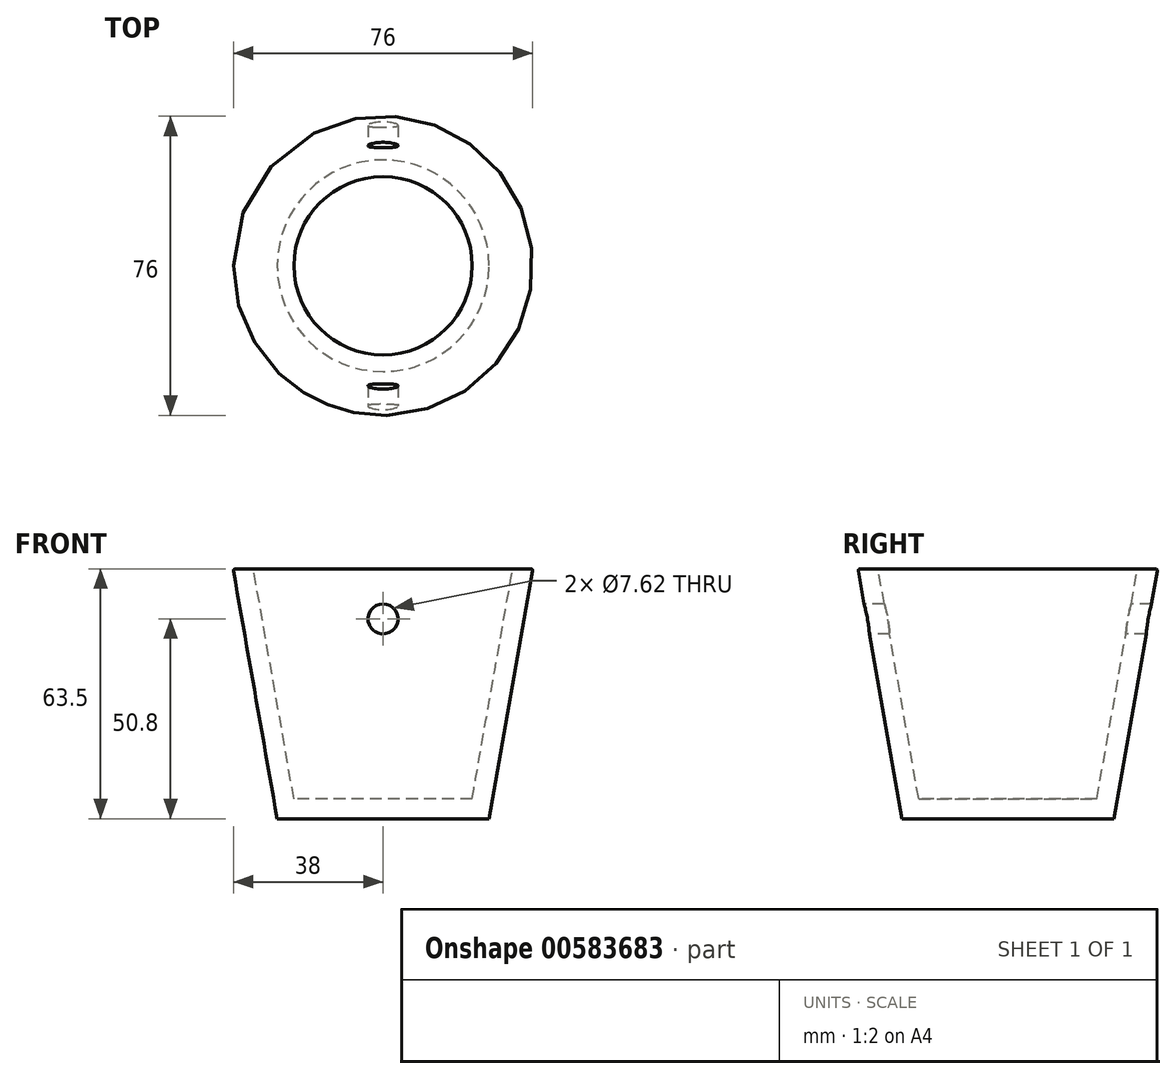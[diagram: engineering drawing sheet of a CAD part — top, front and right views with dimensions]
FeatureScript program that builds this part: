
annotation { "Feature Type Name" : "Feature", "Feature Type Description" : "" }
export const myFeature = defineFeature(function(context is Context, id is Id, definition is map)
    precondition{}
    {
        {
            var Q0;
            Q0=qCreatedBy(makeId("Front.planeOp"),FACE);
            var sketch = newSketch(context, id + "F0", { "sketchPlane" : qUnion([Q0])});
            skLineSegment(sketch, "E0", {"start": v(0, 63.5) * mm, "end": v(-38.1, 63.5) * mm});
            skLineSegment(sketch, "E1", {"start": v(-38.1, 63.5) * mm, "end": v(-26.9, 0) * mm});
            skLineSegment(sketch, "E2", {"start": v(-26.9, 0) * mm, "end": v(0, 0) * mm});
            skLineSegment(sketch, "E3", {"start": v(0, 0) * mm, "end": v(0, 63.5) * mm});
            skSolve(sketch);
        }
        {
            var Q0;
            Q0=makeQuery(id+"F0.imprint","IMPRINT",FACE,{"disambiguationData":[TD([[makeQuery(id+"F0.imprint","IMPRINT",EDGE,{"derivedFrom":sQuery(id+"F0.wireOp",EDGE,"E0")}),1.0]])]});
            var Q1;
            Q1=sQuery(id+"F0.wireOp",EDGE,"E3");
            revolve(context, id + "F1", {"entities" : qUnion([Q0]), "axis" : qUnion([Q1]), "revolveType" : RevolveType.FULL});
        }
        {
            var Q0;
            Q0=makeQuery(id+"F1.opRevolve","SWEPT_FACE",FACE,{"disambiguationData":[OSD([sQuery(id+"F0.wireOp",EDGE,"E0")])]});
            shell(context, id + "F2", {"entities" : qUnion([Q0]), "thickness" : 5.08 * mm});
        }
        {
            var Q0;
            Q0=qCreatedBy(makeId("Front.planeOp"),FACE);
            var sketch = newSketch(context, id + "F3", { "sketchPlane" : qUnion([Q0])});
            skLineSegment(sketch, "E4.0", {"start": v(38.1, 63.5) * mm, "end": v(-38.1, 63.5) * mm});
            skLineSegment(sketch, "E5", {"start": v(0, 63.5) * mm, "end": v(0, 50.8) * mm, "construction": true});
            skCircle(sketch, "E6", {"center": v(0, 50.8) * mm, "radius": 3.81 * mm});
            skSolve(sketch);
        }
        {
            var Q0;
            Q0 = qSketchRegion(id + "F3", true);
            extrude(context, id + "F4", {"entities" : qUnion([Q0]), "operationType" : NewBodyOperationType.REMOVE, "oppositeDirection" : true, "depth" : 50.3 * mm, "offsetDistance" : 25.4 * mm, "hasSecondDirection" : true, "secondDirectionOppositeDirection" : false, "secondDirectionDepth" : 74.17 * mm});
        }
        {
            var Q0;
            Q0=makeQuery(id+"F2.opShell","OFFSET_EDGE",EDGE,{"disambiguationData":[OSD([sQuery(id+"F0.wireOp",EDGE,"E0"),sQuery(id+"F0.wireOp",EDGE,"E1")])]});
            var Q1;
            Q1=makeQuery(id+"F1.opRevolve","SWEPT_EDGE",EDGE,{"disambiguationData":[OSD([sQuery(id+"F0.wireOp",EDGE,"E0"),sQuery(id+"F0.wireOp",EDGE,"E1")])]});
            fillet(context, id + "F5", {"entities" : qUnion([Q0, Q1]), "radius" : 0.5 * mm, "tangentPropagation" : true, "allowEdgeOverflow" : false});
        }
    });
